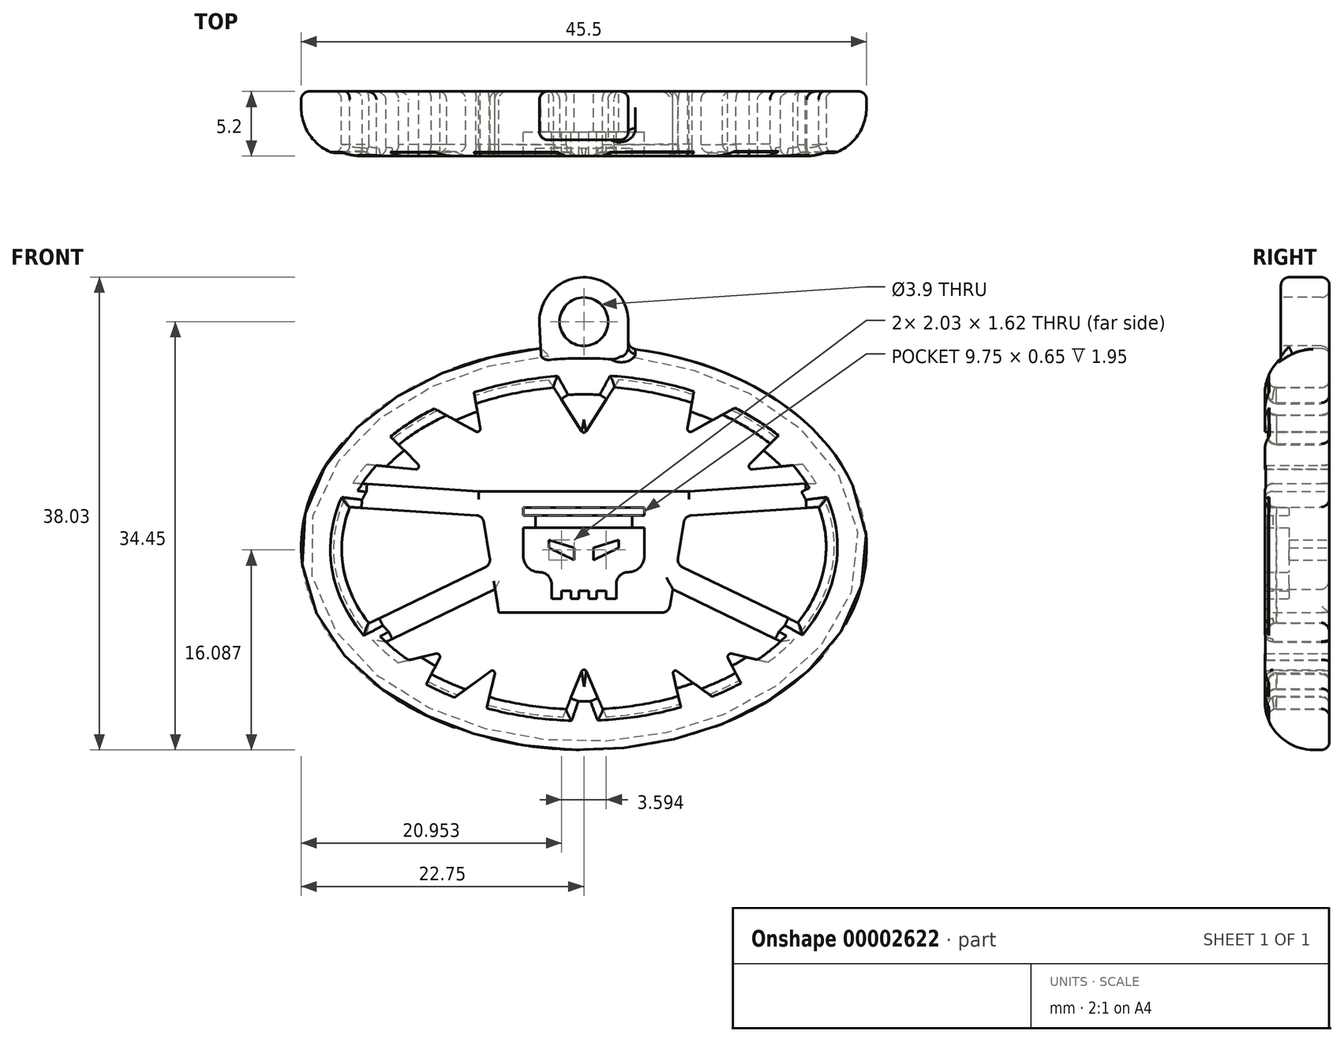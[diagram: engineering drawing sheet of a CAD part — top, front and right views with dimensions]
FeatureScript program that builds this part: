
annotation { "Feature Type Name" : "Feature", "Feature Type Description" : "" }
export const myFeature = defineFeature(function(context is Context, id is Id, definition is map)
    precondition{}
    {
        {
            var Q0;
            Q0=qCreatedBy(makeId("Front.planeOp"),FACE);
            var sketch = newSketch(context, id + "F0", { "sketchPlane" : qUnion([Q0])});
            skEllipse(sketch, "E0", {"center": v(0, 0) * mm, "majorRadius": 17.5 * mm, "minorRadius": 12.5 * mm, "majorAxis": v(1, 0)});
            skEllipticalArc(sketch, "E1", {});
            skLineSegment(sketch, "E2", {"start": v(-6.5, 3.5) * mm, "end": v(-5.27, -4) * mm});
            skLineSegment(sketch, "E3.0.MirrorCS", {"start": v(6.5, 3.5) * mm, "end": v(5.27, -4) * mm});
            skLineSegment(sketch, "E4", {"start": v(-6.5, 3.5) * mm, "end": v(6.5, 3.5) * mm});
            skLineSegment(sketch, "E5", {"start": v(-5.27, -4) * mm, "end": v(5.27, -4) * mm});
            skLineSegment(sketch, "E6", {"start": v(-5.5, -2.56) * mm, "end": v(-12.25, -5.82) * mm});
            skLineSegment(sketch, "E7", {"start": v(-13.3, -4.67) * mm, "end": v(-5.76, -1.02) * mm});
            skLineSegment(sketch, "E8", {"start": v(-6.5, 3.5) * mm, "end": v(-13.72, 3.98) * mm});
            skLineSegment(sketch, "E9", {"start": v(-6.25, 1.98) * mm, "end": v(-14.49, 2.53) * mm});
            skLineSegment(sketch, "E10.0.MirrorCS", {"start": v(6.5, 3.5) * mm, "end": v(13.72, 3.98) * mm});
            skLineSegment(sketch, "E11.0.MirrorCS", {"start": v(6.25, 1.98) * mm, "end": v(14.49, 2.53) * mm});
            skLineSegment(sketch, "E12.0.MirrorCS", {"start": v(13.3, -4.67) * mm, "end": v(5.76, -1.02) * mm});
            skLineSegment(sketch, "E13.0.MirrorCS", {"start": v(5.5, -2.56) * mm, "end": v(12.25, -5.82) * mm});
            skLineSegment(sketch, "E14", {"start": v(0, 2.5) * mm, "end": v(-3.75, 2.5) * mm});
            skLineSegment(sketch, "E15", {"start": v(-3.75, 2.5) * mm, "end": v(-3.75, 2) * mm});
            skLineSegment(sketch, "E16", {"start": v(-3.75, 2) * mm, "end": v(-3, 2) * mm});
            skLineSegment(sketch, "E17", {"start": v(-3, 2) * mm, "end": v(-3, 1.25) * mm});
            skLineSegment(sketch, "E18", {"start": v(-3, 1.25) * mm, "end": v(-3.75, 1.25) * mm});
            skLineSegment(sketch, "E19", {"start": v(-3.75, 1.25) * mm, "end": v(-3.75, -0.5) * mm});
            skLineSegment(sketch, "E20", {"start": v(-2.75, -1.5) * mm, "end": v(-2.75, -1.5) * mm});
            skLineSegment(sketch, "E21", {"start": v(-2, -2.25) * mm, "end": v(-2, -3.16) * mm});
            skLineSegment(sketch, "E22", {"start": v(-2, -3.16) * mm, "end": v(-1.39, -3.16) * mm});
            skLineSegment(sketch, "E23", {"start": v(0, -3.16) * mm, "end": v(0, 2.5) * mm});
            skPoint(sketch, "E24.visualSharp", {"position": v(-3.75, -1.5) * mm});
            skArc(sketch, "E24.filletArc", {"start": v(-3.75, -0.5) * mm, "mid": v(-3.46, -1.2) * mm, "end": v(-2.75, -1.5) * mm});
            skPoint(sketch, "E25.visualSharp", {"position": v(-2, -1.5) * mm});
            skArc(sketch, "E25.filletArc", {"start": v(-2, -2.25) * mm, "mid": v(-2.22, -1.72) * mm, "end": v(-2.75, -1.5) * mm});
            skLineSegment(sketch, "E26.0.MirrorCS", {"start": v(0, 2.5) * mm, "end": v(3.75, 2.5) * mm});
            skLineSegment(sketch, "E27.0.MirrorCS", {"start": v(3.75, 2.5) * mm, "end": v(3.75, 2) * mm});
            skLineSegment(sketch, "E28.0.MirrorCS", {"start": v(3.75, 2) * mm, "end": v(3, 2) * mm});
            skLineSegment(sketch, "E29.0.MirrorCS", {"start": v(3, 2) * mm, "end": v(3, 1.25) * mm});
            skLineSegment(sketch, "E30.0.MirrorCS", {"start": v(3.75, 1.25) * mm, "end": v(3.75, -0.5) * mm});
            skLineSegment(sketch, "E31.0.MirrorCS", {"start": v(3, 1.25) * mm, "end": v(3.75, 1.25) * mm});
            skArc(sketch, "E32.0.MirrorCS", {"start": v(3.75, -0.5) * mm, "mid": v(3.46, -1.2) * mm, "end": v(2.75, -1.5) * mm});
            skArc(sketch, "E33.0.MirrorCS", {"start": v(2, -2.25) * mm, "mid": v(2.22, -1.72) * mm, "end": v(2.75, -1.5) * mm});
            skLineSegment(sketch, "E34.0.MirrorCS", {"start": v(2, -3.16) * mm, "end": v(1.39, -3.16) * mm});
            skLineSegment(sketch, "E35.0.MirrorCS", {"start": v(2, -2.25) * mm, "end": v(2, -3.16) * mm});
            skLineSegment(sketch, "E36", {"start": v(-3, 1.25) * mm, "end": v(3, 1.25) * mm});
            skLineSegment(sketch, "E37", {"start": v(-3, 2) * mm, "end": v(3, 2) * mm});
            skLineSegment(sketch, "E38", {"start": v(-0.6, -0.75) * mm, "end": v(-0.6, 0) * mm});
            skLineSegment(sketch, "E39", {"start": v(-0.6, 0) * mm, "end": v(-2.16, 0.5) * mm});
            skLineSegment(sketch, "E40", {"start": v(-2.16, 0.5) * mm, "end": v(-2.16, 0) * mm});
            skLineSegment(sketch, "E41", {"start": v(-2.16, 0) * mm, "end": v(-0.6, -0.75) * mm});
            skLineSegment(sketch, "E42.0.MirrorCS", {"start": v(0.6, -0.75) * mm, "end": v(0.6, 0) * mm});
            skLineSegment(sketch, "E43.0.MirrorCS", {"start": v(0.6, 0) * mm, "end": v(2.16, 0.5) * mm});
            skLineSegment(sketch, "E44.0.MirrorCS", {"start": v(2.16, 0.5) * mm, "end": v(2.16, 0) * mm});
            skLineSegment(sketch, "E45.0.MirrorCS", {"start": v(2.16, 0) * mm, "end": v(0.6, -0.75) * mm});
            skLineSegment(sketch, "E46.rect.bottom", {"start": v(-0.79, -2.38) * mm, "end": v(-1.39, -2.38) * mm});
            skLineSegment(sketch, "E46.rect.left", {"start": v(-0.79, -2.65) * mm, "end": v(-0.79, -3.16) * mm});
            skLineSegment(sketch, "E46.rect.right", {"start": v(-1.39, -2.65) * mm, "end": v(-1.39, -3.16) * mm});
            skLineSegment(sketch, "E47.trimOffspring", {"start": v(-0.79, -3.16) * mm, "end": v(-0.3, -3.16) * mm});
            skLineSegment(sketch, "E48.0.MirrorCS", {"start": v(1.39, -2.65) * mm, "end": v(1.39, -3.16) * mm});
            skLineSegment(sketch, "E49.0.MirrorCS", {"start": v(0.79, -2.65) * mm, "end": v(0.79, -3.16) * mm});
            skLineSegment(sketch, "E50.trimOffspring", {"start": v(0.79, -3.16) * mm, "end": v(0.3, -3.16) * mm});
            skLineSegment(sketch, "E51.rect.bottom", {"start": v(-0.3, -2.38) * mm, "end": v(0.3, -2.38) * mm});
            skLineSegment(sketch, "E51.rect.left", {"start": v(-0.3, -2.65) * mm, "end": v(-0.3, -3.16) * mm});
            skLineSegment(sketch, "E51.rect.right", {"start": v(0.3, -2.65) * mm, "end": v(0.3, -3.16) * mm});
            skLineSegment(sketch, "E52", {"start": v(13.72, 3.98) * mm, "end": v(13.8, 3.98) * mm});
            skLineSegment(sketch, "E53", {"start": v(14.49, 2.53) * mm, "end": v(14.54, 2.53) * mm});
            skEllipticalArc(sketch, "E54.trimOffspring", {});
            skEllipticalArc(sketch, "E55.trimOffspring", {});
            skEllipticalArc(sketch, "E56.trimOffspring", {});
            skLineSegment(sketch, "E57", {"start": v(-6.68, 8.92) * mm, "end": v(-6.34, 7.01) * mm});
            skLineSegment(sketch, "E58", {"start": v(-6.34, 7.01) * mm, "end": v(-8.5, 8.2) * mm});
            skLineSegment(sketch, "E59", {"start": v(-12.85, 5.1) * mm, "end": v(-9.89, 4.8) * mm});
            skLineSegment(sketch, "E60", {"start": v(-9.89, 4.8) * mm, "end": v(-11.48, 6.39) * mm});
            skLineSegment(sketch, "E61", {"start": v(0, 7.01) * mm, "end": v(-1.86, 9.91) * mm});
            skLineSegment(sketch, "E62.0.MirrorCS", {"start": v(0, 7.01) * mm, "end": v(1.86, 9.91) * mm});
            skLineSegment(sketch, "E63.0.MirrorCS", {"start": v(6.68, 8.92) * mm, "end": v(6.34, 7.01) * mm});
            skLineSegment(sketch, "E64.0.MirrorCS", {"start": v(6.34, 7.01) * mm, "end": v(8.5, 8.2) * mm});
            skLineSegment(sketch, "E65.0.MirrorCS", {"start": v(9.89, 4.8) * mm, "end": v(11.48, 6.39) * mm});
            skLineSegment(sketch, "E66.0.MirrorCS", {"start": v(12.85, 5.1) * mm, "end": v(9.89, 4.8) * mm});
            skLineSegment(sketch, "E67", {"start": v(1.86, 9.91) * mm, "end": v(1.95, 10.06) * mm});
            skLineSegment(sketch, "E68", {"start": v(6.68, 8.92) * mm, "end": v(6.75, 9.33) * mm});
            skLineSegment(sketch, "E69", {"start": v(8.5, 8.2) * mm, "end": v(9, 8.47) * mm});
            skLineSegment(sketch, "E70", {"start": v(11.48, 6.39) * mm, "end": v(11.88, 6.8) * mm});
            skLineSegment(sketch, "E71", {"start": v(12.85, 5.1) * mm, "end": v(13.46, 5.17) * mm});
            skLineSegment(sketch, "E72", {"start": v(-10.85, -6.95) * mm, "end": v(-8.74, -6.45) * mm});
            skLineSegment(sketch, "E73", {"start": v(-8.74, -6.45) * mm, "end": v(-9.44, -7.81) * mm});
            skLineSegment(sketch, "E74", {"start": v(-7.32, -8.76) * mm, "end": v(-5.43, -7.38) * mm});
            skLineSegment(sketch, "E75", {"start": v(-5.43, -7.38) * mm, "end": v(-5.92, -9.51) * mm});
            skLineSegment(sketch, "E76", {"start": v(-1.08, -9.98) * mm, "end": v(0, -7.3) * mm});
            skLineSegment(sketch, "E77", {"start": v(0, -7.3) * mm, "end": v(1.16, -9.96) * mm});
            skLineSegment(sketch, "E78.0.MirrorCS", {"start": v(5.43, -7.38) * mm, "end": v(5.92, -9.51) * mm});
            skLineSegment(sketch, "E79.0.MirrorCS", {"start": v(7.32, -8.76) * mm, "end": v(5.43, -7.38) * mm});
            skLineSegment(sketch, "E80.0.MirrorCS", {"start": v(8.74, -6.45) * mm, "end": v(9.44, -7.81) * mm});
            skLineSegment(sketch, "E81.0.MirrorCS", {"start": v(10.85, -6.95) * mm, "end": v(8.74, -6.45) * mm});
            skArc(sketch, "E82", {"start": v(2.75, 14) * mm, "mid": v(-0.06, 16.75) * mm, "end": v(-2.75, 13.88) * mm});
            skLineSegment(sketch, "E83", {"start": v(-2.75, 13.88) * mm, "end": v(-2.68, 12.35) * mm});
            skLineSegment(sketch, "E84", {"start": v(2.75, 14) * mm, "end": v(2.75, 12.35) * mm});
            skLineSegment(sketch, "E85", {"start": v(-1.39, -2.65) * mm, "end": v(-0.79, -2.65) * mm});
            skLineSegment(sketch, "E86.trimOffspring", {"start": v(-0.3, -2.65) * mm, "end": v(0.3, -2.65) * mm});
            skLineSegment(sketch, "E87.trimOffspring", {"start": v(0.79, -2.65) * mm, "end": v(1.39, -2.65) * mm});
            skPoint(sketch, "E88.orphan", {"position": v(0.79, -2.38) * mm});
            skPoint(sketch, "E89.orphan", {"position": v(1.39, -2.38) * mm});
            const initialGuessF0  = {"E1": [0, 0, 0.9999678975144595, 0.008012736143888071, 0.015, 0.01, 2.8742552580067566, 3.615513402670112], "E54.trimOffspring": [0, 0, 0.9999678975144595, 0.008012736143888071, 0.015, 0.01, 3.751316391230873, 5.653974725832949], "E55.trimOffspring": [0, 0, 0.9999678975144595, 0.008012736143888071, 0.015, 0.01, 5.788912400985266, 0.24363722999687798], "E56.trimOffspring": [0, 0, 0.9999678975144595, 0.008012736143888071, 0.015, 0.01, 0.39710185617883087, 2.7204529747902204]};
            skSetInitialGuess(sketch, initialGuessF0);
            skSolve(sketch);
        }
        {
            var Q0;
            {var subQ8=sQuery(id+"F0.wireOp",EDGE,"E4");Q0=makeQuery(id+"F0.imprint","IMPRINT",FACE,{"disambiguationData":[TD([[makeQuery(id+"F0.imprint","IMPRINT",EDGE,{"derivedFrom":subQ8}),-1.0]])]});}
            var Q1;
            {var subQ1=sQuery(id+"F0.wireOp",EDGE,"E59");Q1=makeQuery(id+"F0.imprint","IMPRINT",FACE,{"disambiguationData":[TD([[makeQuery(id+"F0.imprint","IMPRINT",EDGE,{"derivedFrom":subQ1}),1.0]])]});}
            var Q2;
            {var subQ1=sQuery(id+"F0.wireOp",EDGE,"E57");Q2=makeQuery(id+"F0.imprint","IMPRINT",FACE,{"disambiguationData":[TD([[makeQuery(id+"F0.imprint","IMPRINT",EDGE,{"derivedFrom":subQ1}),-1.0]])]});}
            var Q3;
            {var subQ0=sQuery(id+"F0.wireOp",EDGE,"E61");Q3=makeQuery(id+"F0.imprint","IMPRINT",FACE,{"disambiguationData":[TD([[makeQuery(id+"F0.imprint","IMPRINT",EDGE,{"derivedFrom":subQ0}),-1.0]])]});}
            var Q4;
            {var subQ6=sQuery(id+"F0.wireOp",EDGE,"E63.0.MirrorCS");Q4=makeQuery(id+"F0.imprint","IMPRINT",FACE,{"disambiguationData":[TD([[makeQuery(id+"F0.imprint","IMPRINT",EDGE,{"derivedFrom":subQ6}),1.0]])]});}
            var Q5;
            {var subQ3=sQuery(id+"F0.wireOp",EDGE,"E65.0.MirrorCS");Q5=makeQuery(id+"F0.imprint","IMPRINT",FACE,{"disambiguationData":[TD([[makeQuery(id+"F0.imprint","IMPRINT",EDGE,{"derivedFrom":subQ3}),-1.0]])]});}
            var Q6;
            {var subQ1=sQuery(id+"F0.wireOp",EDGE,"E72");Q6=makeQuery(id+"F0.imprint","IMPRINT",FACE,{"disambiguationData":[TD([[makeQuery(id+"F0.imprint","IMPRINT",EDGE,{"derivedFrom":subQ1}),-1.0]])]});}
            var Q7;
            {var subQ3=sQuery(id+"F0.wireOp",EDGE,"E74");Q7=makeQuery(id+"F0.imprint","IMPRINT",FACE,{"disambiguationData":[TD([[makeQuery(id+"F0.imprint","IMPRINT",EDGE,{"derivedFrom":subQ3}),-1.0]])]});}
            var Q8;
            {var subQ1=sQuery(id+"F0.wireOp",EDGE,"E76");Q8=makeQuery(id+"F0.imprint","IMPRINT",FACE,{"disambiguationData":[TD([[makeQuery(id+"F0.imprint","IMPRINT",EDGE,{"derivedFrom":subQ1}),-1.0]])]});}
            var Q9;
            {var subQ1=sQuery(id+"F0.wireOp",EDGE,"E54.trimOffspring");var subQ3=sQuery(id+"F0.wireOp",EDGE,"E78.0.MirrorCS");var subQ5=makeQuery(id+"F0.imprint","INTERSECT",VERTEX,{"derivedFrom":[subQ1,subQ3]});Q9=makeQuery(id+"F0.imprint","IMPRINT",FACE,{"disambiguationData":[TD([[makeQuery(id+"F0.imprint","IMPRINT",EDGE,{"disambiguationData":[TD([[subQ5,-1.0]])],"derivedFrom":subQ1}),1.0]])]});}
            var Q10;
            {var subQ1=sQuery(id+"F0.wireOp",EDGE,"E54.trimOffspring");var subQ3=sQuery(id+"F0.wireOp",EDGE,"E80.0.MirrorCS");var subQ5=makeQuery(id+"F0.imprint","INTERSECT",VERTEX,{"derivedFrom":[subQ1,subQ3]});Q10=makeQuery(id+"F0.imprint","IMPRINT",FACE,{"disambiguationData":[TD([[makeQuery(id+"F0.imprint","IMPRINT",EDGE,{"disambiguationData":[TD([[subQ5,-1.0]])],"derivedFrom":subQ1}),1.0]])]});}
            var Q11;
            Q11=makeQuery(id+"F0.imprint","IMPRINT",FACE,{"disambiguationData":[TD([[makeQuery(id+"F0.imprint","IMPRINT",EDGE,{"derivedFrom":sQuery(id+"F0.wireOp",EDGE,"E1")}),-1.0]])]});
            var Q12;
            {var subQ1=sQuery(id+"F0.wireOp",EDGE,"E0");var subQ4=makeQuery(id+"F0.imprint","INTERSECT",VERTEX,{"derivedFrom":[subQ1,sQuery(id+"F0.wireOp",EDGE,"6e1ee741-4015-48c1-b213-584f40299b3e")]});Q12=makeQuery(id+"F0.imprint","IMPRINT",FACE,{"disambiguationData":[TD([[makeQuery(id+"F0.imprint","IMPRINT",EDGE,{"disambiguationData":[TD([[subQ4,1.0]])],"derivedFrom":subQ1}),1.0]])]});}
            extrude(context, id + "F1", {"entities" : qUnion([Q0, Q1, Q2, Q3, Q4, Q5, Q6, Q7, Q8, Q9, Q10, Q11, Q12]), "depth" : 4 * mm});
        }
        {
            var Q0;
            {var subQ6=sQuery(id+"F0.wireOp",EDGE,"E18");Q0=makeQuery(id+"F0.imprint","IMPRINT",FACE,{"disambiguationData":[TD([[makeQuery(id+"F0.imprint","IMPRINT",EDGE,{"derivedFrom":subQ6}),1.0]])]});}
            var Q1;
            Q1=makeQuery(id+"F0.imprint","IMPRINT",FACE,{"disambiguationData":[TD([[makeQuery(id+"F0.imprint","IMPRINT",EDGE,{"derivedFrom":sQuery(id+"F0.wireOp",EDGE,"E30.0.MirrorCS")}),-1.0]])]});
            var Q2;
            {var subQ1=sQuery(id+"F0.wireOp",EDGE,"E26.0.MirrorCS");Q2=makeQuery(id+"F0.imprint","IMPRINT",FACE,{"disambiguationData":[TD([[makeQuery(id+"F0.imprint","IMPRINT",EDGE,{"derivedFrom":subQ1}),-1.0]])]});}
            var Q3;
            {var subQ4=sQuery(id+"F0.wireOp",EDGE,"E14");Q3=makeQuery(id+"F0.imprint","IMPRINT",FACE,{"disambiguationData":[TD([[makeQuery(id+"F0.imprint","IMPRINT",EDGE,{"derivedFrom":subQ4}),1.0]])]});}
            extrude(context, id + "F2", {"entities" : qUnion([Q0, Q1, Q2, Q3]), "operationType" : NewBodyOperationType.ADD, "depth" : 2.5 * mm});
        }
        {
            var Q0;
            Q0=makeQuery(id+"F0.imprint","IMPRINT",FACE,{"disambiguationData":[TD([[makeQuery(id+"F0.imprint","IMPRINT",EDGE,{"derivedFrom":sQuery(id+"F0.wireOp",EDGE,"E82")}),1.0]])]});
            extrude(context, id + "F3", {"entities" : qUnion([Q0]), "operationType" : NewBodyOperationType.ADD, "depth" : 3 * mm});
        }
        {
            var Q0;
            Q0=makeQuery(id+"F3.opExtrude","CAP_FACE",FACE,{"disambiguationData":[OSD([sQuery(id+"F0.wireOp",EDGE,"E0"),sQuery(id+"F0.wireOp",EDGE,"E82"),sQuery(id+"F0.wireOp",EDGE,"E83"),sQuery(id+"F0.wireOp",EDGE,"E84")])],"isStart":false});
            var sketch = newSketch(context, id + "F4", { "sketchPlane" : qUnion([Q0])});
            skCircle(sketch, "E90", {"center": v(0, 14) * mm, "radius": 1.5 * mm});
            skSolve(sketch);
        }
        {
            var Q0;
            Q0=makeQuery(id+"F4.imprint","IMPRINT",FACE,{"disambiguationData":[TD([[makeQuery(id+"F4.imprint","IMPRINT",EDGE,{"derivedFrom":sQuery(id+"F4.wireOp",EDGE,"E90")}),1.0]])]});
            extrude(context, id + "F5", {"entities" : qUnion([Q0]), "operationType" : NewBodyOperationType.REMOVE, "oppositeDirection" : true, "depth" : 25 * mm});
        }
        {
            var Q0;
            Q0=makeQuery(id+"F1.opExtrude","CAP_EDGE",EDGE,{"disambiguationData":[OSD([sQuery(id+"F0.wireOp",EDGE,"E0")])],"isStart":false});
            fillet(context, id + "F6", {"entities" : qUnion([Q0]), "radius" : 3 * mm, "tangentPropagation" : true, "allowEdgeOverflow" : false});
        }
        {
            var Q0;
            Q0=makeQuery(id+"F1.opExtrude","CAP_EDGE",EDGE,{"disambiguationData":[OSD([sQuery(id+"F0.wireOp",EDGE,"E0")])],"isStart":true});
            var Q1;
            Q1=makeQuery(id+"F3.opExtrude","CAP_EDGE",EDGE,{"disambiguationData":[OSD([sQuery(id+"F0.wireOp",EDGE,"E82")])],"isStart":true});
            var Q2;
            Q2=makeQuery(id+"F3.opExtrude","CAP_EDGE",EDGE,{"disambiguationData":[OSD([sQuery(id+"F0.wireOp",EDGE,"E84")])],"isStart":true});
            var Q3;
            Q3=makeQuery(id+"F3.opExtrude","CAP_EDGE",EDGE,{"disambiguationData":[OSD([sQuery(id+"F0.wireOp",EDGE,"E83")])],"isStart":true});
            var Q4;
            Q4=makeQuery(id+"F3.opExtrude","CAP_EDGE",EDGE,{"disambiguationData":[OSD([sQuery(id+"F0.wireOp",EDGE,"E82")])],"isStart":false});
            var Q5;
            Q5=makeQuery(id+"F3.opExtrude","CAP_EDGE",EDGE,{"disambiguationData":[OSD([sQuery(id+"F0.wireOp",EDGE,"E84")])],"isStart":false});
            var Q6;
            Q6=makeQuery(id+"F6.opFillet","BLEND_EDGE",EDGE,{"blendedFrom":[makeQuery(id+"F1.opExtrude","CAP_EDGE",EDGE,{"disambiguationData":[OSD([sQuery(id+"F0.wireOp",EDGE,"E0")])],"isStart":false}),makeQuery(id+"F3.opExtrude","SWEPT_FACE",FACE,{"disambiguationData":[OSD([sQuery(id+"F0.wireOp",EDGE,"E84")])]})],"blendedInto":[makeQuery(id+"F3.opExtrude","SWEPT_FACE",FACE,{"disambiguationData":[OSD([sQuery(id+"F0.wireOp",EDGE,"E84")])]})]});
            var Q7;
            {var subQ0=sQuery(id+"F0.wireOp",EDGE,"E0");var subQ1=sQuery(id+"F0.wireOp",EDGE,"E14");var subQ2=sQuery(id+"F0.wireOp",EDGE,"E15");var subQ3=sQuery(id+"F0.wireOp",EDGE,"E16");var subQ4=sQuery(id+"F0.wireOp",EDGE,"E18");var subQ5=sQuery(id+"F0.wireOp",EDGE,"E19");var subQ6=sQuery(id+"F0.wireOp",EDGE,"E21");var subQ7=sQuery(id+"F0.wireOp",EDGE,"E22");var subQ8=sQuery(id+"F0.wireOp",EDGE,"E24.filletArc");var subQ9=sQuery(id+"F0.wireOp",EDGE,"E25.filletArc");var subQ10=sQuery(id+"F0.wireOp",EDGE,"E26.0.MirrorCS");var subQ11=sQuery(id+"F0.wireOp",EDGE,"E27.0.MirrorCS");var subQ12=sQuery(id+"F0.wireOp",EDGE,"E28.0.MirrorCS");var subQ13=sQuery(id+"F0.wireOp",EDGE,"E30.0.MirrorCS");var subQ14=sQuery(id+"F0.wireOp",EDGE,"E31.0.MirrorCS");var subQ15=sQuery(id+"F0.wireOp",EDGE,"E32.0.MirrorCS");var subQ16=sQuery(id+"F0.wireOp",EDGE,"E33.0.MirrorCS");var subQ17=sQuery(id+"F0.wireOp",EDGE,"E34.0.MirrorCS");var subQ18=sQuery(id+"F0.wireOp",EDGE,"E35.0.MirrorCS");var subQ19=sQuery(id+"F0.wireOp",EDGE,"E46.rect.left");var subQ20=sQuery(id+"F0.wireOp",EDGE,"E46.rect.right");var subQ21=sQuery(id+"F0.wireOp",EDGE,"E47.trimOffspring");var subQ22=sQuery(id+"F0.wireOp",EDGE,"E48.0.MirrorCS");var subQ23=sQuery(id+"F0.wireOp",EDGE,"E49.0.MirrorCS");var subQ24=sQuery(id+"F0.wireOp",EDGE,"E50.trimOffspring");var subQ25=sQuery(id+"F0.wireOp",EDGE,"E51.rect.left");var subQ26=sQuery(id+"F0.wireOp",EDGE,"E51.rect.right");var subQ27=sQuery(id+"F0.wireOp",EDGE,"E85");var subQ28=sQuery(id+"F0.wireOp",EDGE,"E86.trimOffspring");var subQ29=sQuery(id+"F0.wireOp",EDGE,"E87.trimOffspring");Q7=makeQuery(id+"F5.boolean.opBoolean","INTERSECT",EDGE,{"derivedFrom":[makeQuery(id+"F3.boolean.opBoolean","MERGE",FACE,{"derivedFrom":[makeQuery(id+"F2.boolean.opBoolean","MERGE",FACE,{"derivedFrom":[makeQuery(id+"F1.opExtrude","CAP_FACE",FACE,{"disambiguationData":[OSD([subQ0,sQuery(id+"F0.wireOp",EDGE,"E1"),sQuery(id+"F0.wireOp",EDGE,"E2"),sQuery(id+"F0.wireOp",EDGE,"E3.0.MirrorCS"),sQuery(id+"F0.wireOp",EDGE,"E4"),sQuery(id+"F0.wireOp",EDGE,"E5"),sQuery(id+"F0.wireOp",EDGE,"E6"),sQuery(id+"F0.wireOp",EDGE,"E7"),sQuery(id+"F0.wireOp",EDGE,"E8"),sQuery(id+"F0.wireOp",EDGE,"E9"),sQuery(id+"F0.wireOp",EDGE,"E10.0.MirrorCS"),sQuery(id+"F0.wireOp",EDGE,"E11.0.MirrorCS"),sQuery(id+"F0.wireOp",EDGE,"E12.0.MirrorCS"),sQuery(id+"F0.wireOp",EDGE,"E13.0.MirrorCS"),subQ1,subQ2,subQ3,sQuery(id+"F0.wireOp",EDGE,"E17"),subQ4,subQ5,subQ6,subQ7,subQ8,subQ9,subQ10,subQ11,subQ12,sQuery(id+"F0.wireOp",EDGE,"E29.0.MirrorCS"),subQ13,subQ14,subQ15,subQ16,subQ17,subQ18,subQ19,subQ20,subQ21,subQ22,subQ23,subQ24,subQ25,subQ26,sQuery(id+"F0.wireOp",EDGE,"E52"),sQuery(id+"F0.wireOp",EDGE,"E53"),sQuery(id+"F0.wireOp",EDGE,"E54.trimOffspring"),sQuery(id+"F0.wireOp",EDGE,"E55.trimOffspring"),sQuery(id+"F0.wireOp",EDGE,"E56.trimOffspring"),sQuery(id+"F0.wireOp",EDGE,"E57"),sQuery(id+"F0.wireOp",EDGE,"E58"),sQuery(id+"F0.wireOp",EDGE,"E59"),sQuery(id+"F0.wireOp",EDGE,"E60"),sQuery(id+"F0.wireOp",EDGE,"E61"),sQuery(id+"F0.wireOp",EDGE,"E62.0.MirrorCS"),sQuery(id+"F0.wireOp",EDGE,"E63.0.MirrorCS"),sQuery(id+"F0.wireOp",EDGE,"E64.0.MirrorCS"),sQuery(id+"F0.wireOp",EDGE,"E65.0.MirrorCS"),sQuery(id+"F0.wireOp",EDGE,"E66.0.MirrorCS"),sQuery(id+"F0.wireOp",EDGE,"E67"),sQuery(id+"F0.wireOp",EDGE,"E68"),sQuery(id+"F0.wireOp",EDGE,"E69"),sQuery(id+"F0.wireOp",EDGE,"E70"),sQuery(id+"F0.wireOp",EDGE,"E71"),sQuery(id+"F0.wireOp",EDGE,"E72"),sQuery(id+"F0.wireOp",EDGE,"E73"),sQuery(id+"F0.wireOp",EDGE,"E74"),sQuery(id+"F0.wireOp",EDGE,"E75"),sQuery(id+"F0.wireOp",EDGE,"E76"),sQuery(id+"F0.wireOp",EDGE,"E77"),sQuery(id+"F0.wireOp",EDGE,"E78.0.MirrorCS"),sQuery(id+"F0.wireOp",EDGE,"E79.0.MirrorCS"),sQuery(id+"F0.wireOp",EDGE,"E80.0.MirrorCS"),sQuery(id+"F0.wireOp",EDGE,"E81.0.MirrorCS"),subQ27,subQ28,subQ29])],"isStart":true}),makeQuery(id+"F2.opExtrude","CAP_FACE",FACE,{"disambiguationData":[OSD([subQ1,subQ2,subQ3,subQ10,subQ11,subQ12,sQuery(id+"F0.wireOp",EDGE,"E37")])],"isStart":true}),makeQuery(id+"F2.opExtrude","CAP_FACE",FACE,{"disambiguationData":[OSD([subQ4,subQ5,subQ6,subQ7,subQ8,subQ9,subQ13,subQ14,subQ15,subQ16,subQ17,subQ18,sQuery(id+"F0.wireOp",EDGE,"E36"),sQuery(id+"F0.wireOp",EDGE,"E38"),sQuery(id+"F0.wireOp",EDGE,"E39"),sQuery(id+"F0.wireOp",EDGE,"E40"),sQuery(id+"F0.wireOp",EDGE,"E41"),sQuery(id+"F0.wireOp",EDGE,"E42.0.MirrorCS"),sQuery(id+"F0.wireOp",EDGE,"E43.0.MirrorCS"),sQuery(id+"F0.wireOp",EDGE,"E44.0.MirrorCS"),sQuery(id+"F0.wireOp",EDGE,"E45.0.MirrorCS"),subQ19,subQ20,subQ21,subQ22,subQ23,subQ24,subQ25,subQ26,subQ27,subQ28,subQ29])],"isStart":true})]}),makeQuery(id+"F3.opExtrude","CAP_FACE",FACE,{"disambiguationData":[OSD([subQ0,sQuery(id+"F0.wireOp",EDGE,"E82"),sQuery(id+"F0.wireOp",EDGE,"E83"),sQuery(id+"F0.wireOp",EDGE,"E84")])],"isStart":true})]}),makeQuery(id+"F5.opExtrude","SWEPT_FACE",FACE,{"disambiguationData":[OSD([sQuery(id+"F4.wireOp",EDGE,"E90")])]})]});}
            var Q8;
            Q8=makeQuery(id+"F5.boolean.opBoolean","COPY",EDGE,{"derivedFrom":makeQuery(id+"F5.opExtrude","CAP_EDGE",EDGE,{"disambiguationData":[OSD([sQuery(id+"F4.wireOp",EDGE,"E90")])],"isStart":true})});
            var Q9;
            Q9=makeQuery(id+"F1.opExtrude","CAP_EDGE",EDGE,{"disambiguationData":[OSD([sQuery(id+"F0.wireOp",EDGE,"E7")])],"isStart":false});
            var Q10;
            Q10=makeQuery(id+"F1.opExtrude","CAP_EDGE",EDGE,{"disambiguationData":[OSD([sQuery(id+"F0.wireOp",EDGE,"E9")])],"isStart":true});
            var Q11;
            Q11=makeQuery(id+"F1.opExtrude","CAP_EDGE",EDGE,{"disambiguationData":[OSD([sQuery(id+"F0.wireOp",EDGE,"E8")])],"isStart":false});
            var Q12;
            Q12=makeQuery(id+"F1.opExtrude","CAP_EDGE",EDGE,{"disambiguationData":[OSD([sQuery(id+"F0.wireOp",EDGE,"E4")])],"isStart":false});
            var Q13;
            Q13=makeQuery(id+"F1.opExtrude","CAP_EDGE",EDGE,{"disambiguationData":[OSD([sQuery(id+"F0.wireOp",EDGE,"E10.0.MirrorCS")])],"isStart":false});
            var Q14;
            Q14=makeQuery(id+"F1.opExtrude","CAP_EDGE",EDGE,{"disambiguationData":[OSD([sQuery(id+"F0.wireOp",EDGE,"E11.0.MirrorCS"),sQuery(id+"F0.wireOp",EDGE,"E53")])],"isStart":false});
            var Q15;
            {var subQ0=sQuery(id+"F0.wireOp",EDGE,"E3.0.MirrorCS");Q15=makeQuery(id+"F1.opExtrude","CAP_EDGE",EDGE,{"disambiguationData":[OSD([subQ0]),TDD([makeQuery(id+"F0.imprint","IMPRINT",EDGE,{"disambiguationData":[TD([[makeQuery(id+"F0.imprint","INTERSECT",VERTEX,{"derivedFrom":[subQ0,sQuery(id+"F0.wireOp",EDGE,"E11.0.MirrorCS")]}),-1.0]])],"derivedFrom":subQ0})])],"isStart":false});}
            var Q16;
            Q16=makeQuery(id+"F1.opExtrude","CAP_EDGE",EDGE,{"disambiguationData":[OSD([sQuery(id+"F0.wireOp",EDGE,"E12.0.MirrorCS")])],"isStart":true});
            var Q17;
            Q17=makeQuery(id+"F1.opExtrude","CAP_EDGE",EDGE,{"disambiguationData":[OSD([sQuery(id+"F0.wireOp",EDGE,"E13.0.MirrorCS")])],"isStart":false});
            var Q18;
            {var subQ0=sQuery(id+"F0.wireOp",EDGE,"E3.0.MirrorCS");Q18=makeQuery(id+"F1.opExtrude","CAP_EDGE",EDGE,{"disambiguationData":[OSD([subQ0]),TDD([makeQuery(id+"F0.imprint","IMPRINT",EDGE,{"disambiguationData":[TD([[makeQuery(id+"F0.imprint","INTERSECT",VERTEX,{"derivedFrom":[subQ0,sQuery(id+"F0.wireOp",EDGE,"E5")]}),1.0]])],"derivedFrom":subQ0})])],"isStart":false});}
            var Q19;
            Q19=makeQuery(id+"F1.opExtrude","CAP_EDGE",EDGE,{"disambiguationData":[OSD([sQuery(id+"F0.wireOp",EDGE,"E5")])],"isStart":false});
            var Q20;
            Q20=makeQuery(id+"F1.opExtrude","SWEPT_EDGE",EDGE,{"disambiguationData":[OSD([sQuery(id+"F0.wireOp",EDGE,"E3.0.MirrorCS"),sQuery(id+"F0.wireOp",EDGE,"E5")])]});
            var Q21;
            {var subQ0=sQuery(id+"F0.wireOp",EDGE,"E3.0.MirrorCS");Q21=makeQuery(id+"F1.opExtrude","CAP_EDGE",EDGE,{"disambiguationData":[OSD([subQ0]),TDD([makeQuery(id+"F0.imprint","IMPRINT",EDGE,{"disambiguationData":[TD([[makeQuery(id+"F0.imprint","INTERSECT",VERTEX,{"derivedFrom":[subQ0,sQuery(id+"F0.wireOp",EDGE,"E11.0.MirrorCS")]}),-1.0]])],"derivedFrom":subQ0})])],"isStart":true});}
            var Q22;
            {var subQ0=sQuery(id+"F0.wireOp",EDGE,"E3.0.MirrorCS");Q22=makeQuery(id+"F1.opExtrude","CAP_EDGE",EDGE,{"disambiguationData":[OSD([subQ0]),TDD([makeQuery(id+"F0.imprint","IMPRINT",EDGE,{"disambiguationData":[TD([[makeQuery(id+"F0.imprint","INTERSECT",VERTEX,{"derivedFrom":[subQ0,sQuery(id+"F0.wireOp",EDGE,"E5")]}),1.0]])],"derivedFrom":subQ0})])],"isStart":true});}
            var Q23;
            Q23=makeQuery(id+"F1.opExtrude","CAP_EDGE",EDGE,{"disambiguationData":[OSD([sQuery(id+"F0.wireOp",EDGE,"E6")])],"isStart":true});
            var Q24;
            Q24=makeQuery(id+"F1.opExtrude","CAP_EDGE",EDGE,{"disambiguationData":[OSD([sQuery(id+"F0.wireOp",EDGE,"E6")])],"isStart":false});
            var Q25;
            Q25=makeQuery(id+"F1.opExtrude","CAP_EDGE",EDGE,{"disambiguationData":[OSD([sQuery(id+"F0.wireOp",EDGE,"E11.0.MirrorCS"),sQuery(id+"F0.wireOp",EDGE,"E53")])],"isStart":true});
            var Q26;
            Q26=makeQuery(id+"F6.opFillet","BLEND_EDGE",EDGE,{"blendedFrom":[makeQuery(id+"F1.opExtrude","CAP_EDGE",EDGE,{"disambiguationData":[OSD([sQuery(id+"F0.wireOp",EDGE,"E0")])],"isStart":false}),makeQuery(id+"F1.opExtrude","SWEPT_FACE",FACE,{"disambiguationData":[OSD([sQuery(id+"F0.wireOp",EDGE,"E55.trimOffspring")])]})],"blendedInto":[makeQuery(id+"F1.opExtrude","SWEPT_FACE",FACE,{"disambiguationData":[OSD([sQuery(id+"F0.wireOp",EDGE,"E55.trimOffspring")])]})]});
            var Q27;
            Q27=makeQuery(id+"F1.opExtrude","CAP_EDGE",EDGE,{"disambiguationData":[OSD([sQuery(id+"F0.wireOp",EDGE,"E12.0.MirrorCS")])],"isStart":false});
            var Q28;
            Q28=makeQuery(id+"F1.opExtrude","CAP_EDGE",EDGE,{"disambiguationData":[OSD([sQuery(id+"F0.wireOp",EDGE,"E9")])],"isStart":false});
            var Q29;
            Q29=makeQuery(id+"F1.opExtrude","CAP_EDGE",EDGE,{"disambiguationData":[OSD([sQuery(id+"F0.wireOp",EDGE,"E7")])],"isStart":true});
            var Q30;
            Q30=makeQuery(id+"F1.opExtrude","CAP_EDGE",EDGE,{"disambiguationData":[OSD([sQuery(id+"F0.wireOp",EDGE,"E55.trimOffspring")])],"isStart":true});
            var Q31;
            {var subQ0=sQuery(id+"F0.wireOp",EDGE,"E56.trimOffspring");Q31=makeQuery(id+"F1.opExtrude","CAP_EDGE",EDGE,{"disambiguationData":[OSD([subQ0]),TDD([makeQuery(id+"F0.imprint","IMPRINT",EDGE,{"disambiguationData":[TD([[makeQuery(id+"F0.imprint","INTERSECT",VERTEX,{"derivedFrom":[subQ0,sQuery(id+"F0.wireOp",EDGE,"E70")]}),-1.0]])],"derivedFrom":subQ0})])],"isStart":true});}
            var Q32;
            {var subQ0=sQuery(id+"F0.wireOp",EDGE,"E56.trimOffspring");Q32=makeQuery(id+"F1.opExtrude","CAP_EDGE",EDGE,{"disambiguationData":[OSD([subQ0]),TDD([makeQuery(id+"F0.imprint","IMPRINT",EDGE,{"disambiguationData":[TD([[makeQuery(id+"F0.imprint","INTERSECT",VERTEX,{"derivedFrom":[subQ0,sQuery(id+"F0.wireOp",EDGE,"E68")]}),-1.0]])],"derivedFrom":subQ0})])],"isStart":true});}
            var Q33;
            {var subQ0=sQuery(id+"F0.wireOp",EDGE,"E56.trimOffspring");Q33=makeQuery(id+"F1.opExtrude","CAP_EDGE",EDGE,{"disambiguationData":[OSD([subQ0]),TDD([makeQuery(id+"F0.imprint","IMPRINT",EDGE,{"disambiguationData":[TD([[makeQuery(id+"F0.imprint","INTERSECT",VERTEX,{"derivedFrom":[subQ0,sQuery(id+"F0.wireOp",EDGE,"E57")]}),1.0]])],"derivedFrom":subQ0})])],"isStart":true});}
            var Q34;
            {var subQ0=sQuery(id+"F0.wireOp",EDGE,"E56.trimOffspring");Q34=makeQuery(id+"F1.opExtrude","CAP_EDGE",EDGE,{"disambiguationData":[OSD([subQ0]),TDD([makeQuery(id+"F0.imprint","IMPRINT",EDGE,{"disambiguationData":[TD([[makeQuery(id+"F0.imprint","INTERSECT",VERTEX,{"derivedFrom":[subQ0,sQuery(id+"F0.wireOp",EDGE,"E58")]}),-1.0]])],"derivedFrom":subQ0})])],"isStart":true});}
            var Q35;
            {var subQ0=sQuery(id+"F0.wireOp",EDGE,"E56.trimOffspring");Q35=makeQuery(id+"F1.opExtrude","CAP_EDGE",EDGE,{"disambiguationData":[OSD([subQ0]),TDD([makeQuery(id+"F0.imprint","IMPRINT",EDGE,{"disambiguationData":[TD([[makeQuery(id+"F0.imprint","INTERSECT",VERTEX,{"derivedFrom":[sQuery(id+"F0.wireOp",EDGE,"E8"),subQ0]}),1.0]])],"derivedFrom":subQ0})])],"isStart":true});}
            var Q36;
            {var subQ0=sQuery(id+"F0.wireOp",EDGE,"E56.trimOffspring");Q36=makeQuery(id+"F1.opExtrude","CAP_EDGE",EDGE,{"disambiguationData":[OSD([subQ0]),TDD([makeQuery(id+"F0.imprint","IMPRINT",EDGE,{"disambiguationData":[TD([[makeQuery(id+"F0.imprint","INTERSECT",VERTEX,{"derivedFrom":[sQuery(id+"F0.wireOp",EDGE,"E52"),subQ0]}),-1.0]])],"derivedFrom":subQ0})])],"isStart":true});}
            var Q37;
            {var subQ0=sQuery(id+"F0.wireOp",EDGE,"E54.trimOffspring");Q37=makeQuery(id+"F1.opExtrude","CAP_EDGE",EDGE,{"disambiguationData":[OSD([subQ0]),TDD([makeQuery(id+"F0.imprint","IMPRINT",EDGE,{"disambiguationData":[TD([[makeQuery(id+"F0.imprint","INTERSECT",VERTEX,{"derivedFrom":[sQuery(id+"F0.wireOp",EDGE,"E13.0.MirrorCS"),subQ0]}),1.0]])],"derivedFrom":subQ0})])],"isStart":true});}
            var Q38;
            {var subQ0=sQuery(id+"F0.wireOp",EDGE,"E54.trimOffspring");Q38=makeQuery(id+"F1.opExtrude","CAP_EDGE",EDGE,{"disambiguationData":[OSD([subQ0]),TDD([makeQuery(id+"F0.imprint","IMPRINT",EDGE,{"disambiguationData":[TD([[makeQuery(id+"F0.imprint","INTERSECT",VERTEX,{"derivedFrom":[subQ0,sQuery(id+"F0.wireOp",EDGE,"E79.0.MirrorCS")]}),-1.0]])],"derivedFrom":subQ0})])],"isStart":true});}
            var Q39;
            {var subQ0=sQuery(id+"F0.wireOp",EDGE,"E54.trimOffspring");Q39=makeQuery(id+"F1.opExtrude","CAP_EDGE",EDGE,{"disambiguationData":[OSD([subQ0]),TDD([makeQuery(id+"F0.imprint","IMPRINT",EDGE,{"disambiguationData":[TD([[makeQuery(id+"F0.imprint","INTERSECT",VERTEX,{"derivedFrom":[subQ0,sQuery(id+"F0.wireOp",EDGE,"E77")]}),-1.0]])],"derivedFrom":subQ0})])],"isStart":true});}
            var Q40;
            {var subQ0=sQuery(id+"F0.wireOp",EDGE,"E54.trimOffspring");Q40=makeQuery(id+"F1.opExtrude","CAP_EDGE",EDGE,{"disambiguationData":[OSD([subQ0]),TDD([makeQuery(id+"F0.imprint","IMPRINT",EDGE,{"disambiguationData":[TD([[makeQuery(id+"F0.imprint","INTERSECT",VERTEX,{"derivedFrom":[subQ0,sQuery(id+"F0.wireOp",EDGE,"E76")]}),1.0]])],"derivedFrom":subQ0})])],"isStart":true});}
            var Q41;
            {var subQ0=sQuery(id+"F0.wireOp",EDGE,"E54.trimOffspring");Q41=makeQuery(id+"F1.opExtrude","CAP_EDGE",EDGE,{"disambiguationData":[OSD([subQ0]),TDD([makeQuery(id+"F0.imprint","IMPRINT",EDGE,{"disambiguationData":[TD([[makeQuery(id+"F0.imprint","INTERSECT",VERTEX,{"derivedFrom":[subQ0,sQuery(id+"F0.wireOp",EDGE,"E73")]}),-1.0]])],"derivedFrom":subQ0})])],"isStart":true});}
            var Q42;
            {var subQ0=sQuery(id+"F0.wireOp",EDGE,"E54.trimOffspring");Q42=makeQuery(id+"F1.opExtrude","CAP_EDGE",EDGE,{"disambiguationData":[OSD([subQ0]),TDD([makeQuery(id+"F0.imprint","IMPRINT",EDGE,{"disambiguationData":[TD([[makeQuery(id+"F0.imprint","INTERSECT",VERTEX,{"derivedFrom":[sQuery(id+"F0.wireOp",EDGE,"E6"),subQ0]}),-1.0]])],"derivedFrom":subQ0})])],"isStart":true});}
            var Q43;
            Q43=makeQuery(id+"F1.opExtrude","CAP_EDGE",EDGE,{"disambiguationData":[OSD([sQuery(id+"F0.wireOp",EDGE,"E1")])],"isStart":true});
            var Q44;
            Q44=makeQuery(id+"F1.opExtrude","CAP_EDGE",EDGE,{"disambiguationData":[OSD([sQuery(id+"F0.wireOp",EDGE,"E13.0.MirrorCS")])],"isStart":true});
            var Q45;
            {var subQ0=sQuery(id+"F0.wireOp",EDGE,"E2");Q45=makeQuery(id+"F1.opExtrude","CAP_EDGE",EDGE,{"disambiguationData":[OSD([subQ0]),TDD([makeQuery(id+"F0.imprint","IMPRINT",EDGE,{"disambiguationData":[TD([[makeQuery(id+"F0.imprint","INTERSECT",VERTEX,{"derivedFrom":[subQ0,sQuery(id+"F0.wireOp",EDGE,"E5")]}),1.0]])],"derivedFrom":subQ0})])],"isStart":true});}
            var Q46;
            {var subQ0=sQuery(id+"F0.wireOp",EDGE,"E2");Q46=makeQuery(id+"F1.opExtrude","CAP_EDGE",EDGE,{"disambiguationData":[OSD([subQ0]),TDD([makeQuery(id+"F0.imprint","IMPRINT",EDGE,{"disambiguationData":[TD([[makeQuery(id+"F0.imprint","INTERSECT",VERTEX,{"derivedFrom":[subQ0,sQuery(id+"F0.wireOp",EDGE,"E7")]}),1.0]])],"derivedFrom":subQ0})])],"isStart":true});}
            var Q47;
            {var subQ0=sQuery(id+"F0.wireOp",EDGE,"E2");Q47=makeQuery(id+"F1.opExtrude","CAP_EDGE",EDGE,{"disambiguationData":[OSD([subQ0]),TDD([makeQuery(id+"F0.imprint","IMPRINT",EDGE,{"disambiguationData":[TD([[makeQuery(id+"F0.imprint","INTERSECT",VERTEX,{"derivedFrom":[subQ0,sQuery(id+"F0.wireOp",EDGE,"E7")]}),1.0]])],"derivedFrom":subQ0})])],"isStart":false});}
            var Q48;
            Q48=makeQuery(id+"F1.opExtrude","SWEPT_EDGE",EDGE,{"disambiguationData":[OSD([sQuery(id+"F0.wireOp",EDGE,"E2"),sQuery(id+"F0.wireOp",EDGE,"E7")])]});
            var Q49;
            Q49=makeQuery(id+"F1.opExtrude","SWEPT_EDGE",EDGE,{"disambiguationData":[OSD([sQuery(id+"F0.wireOp",EDGE,"E3.0.MirrorCS"),sQuery(id+"F0.wireOp",EDGE,"E12.0.MirrorCS")])]});
            var Q50;
            Q50=makeQuery(id+"F1.opExtrude","SWEPT_EDGE",EDGE,{"disambiguationData":[OSD([sQuery(id+"F0.wireOp",EDGE,"E3.0.MirrorCS"),sQuery(id+"F0.wireOp",EDGE,"E11.0.MirrorCS")])]});
            var Q51;
            Q51=makeQuery(id+"F1.opExtrude","SWEPT_EDGE",EDGE,{"disambiguationData":[OSD([sQuery(id+"F0.wireOp",EDGE,"E2"),sQuery(id+"F0.wireOp",EDGE,"E9")])]});
            var Q52;
            {var subQ0=sQuery(id+"F0.wireOp",EDGE,"E56.trimOffspring");Q52=makeQuery(id+"F6.opFillet","BLEND_EDGE",EDGE,{"blendedFrom":[makeQuery(id+"F1.opExtrude","CAP_EDGE",EDGE,{"disambiguationData":[OSD([sQuery(id+"F0.wireOp",EDGE,"E0")])],"isStart":false}),makeQuery(id+"F1.opExtrude","SWEPT_FACE",FACE,{"disambiguationData":[OSD([subQ0]),TDD([makeQuery(id+"F0.imprint","IMPRINT",EDGE,{"disambiguationData":[TD([[makeQuery(id+"F0.imprint","INTERSECT",VERTEX,{"derivedFrom":[subQ0,sQuery(id+"F0.wireOp",EDGE,"E58")]}),-1.0]])],"derivedFrom":subQ0})])]})],"blendedInto":[makeQuery(id+"F1.opExtrude","SWEPT_FACE",FACE,{"disambiguationData":[OSD([subQ0]),TDD([makeQuery(id+"F0.imprint","IMPRINT",EDGE,{"disambiguationData":[TD([[makeQuery(id+"F0.imprint","INTERSECT",VERTEX,{"derivedFrom":[subQ0,sQuery(id+"F0.wireOp",EDGE,"E58")]}),-1.0]])],"derivedFrom":subQ0})])]})]});}
            var Q53;
            {var subQ0=sQuery(id+"F0.wireOp",EDGE,"E56.trimOffspring");Q53=makeQuery(id+"F6.opFillet","BLEND_EDGE",EDGE,{"blendedFrom":[makeQuery(id+"F1.opExtrude","CAP_EDGE",EDGE,{"disambiguationData":[OSD([sQuery(id+"F0.wireOp",EDGE,"E0")])],"isStart":false}),makeQuery(id+"F1.opExtrude","SWEPT_FACE",FACE,{"disambiguationData":[OSD([subQ0]),TDD([makeQuery(id+"F0.imprint","IMPRINT",EDGE,{"disambiguationData":[TD([[makeQuery(id+"F0.imprint","INTERSECT",VERTEX,{"derivedFrom":[subQ0,sQuery(id+"F0.wireOp",EDGE,"E57")]}),1.0]])],"derivedFrom":subQ0})])]})],"blendedInto":[makeQuery(id+"F1.opExtrude","SWEPT_FACE",FACE,{"disambiguationData":[OSD([subQ0]),TDD([makeQuery(id+"F0.imprint","IMPRINT",EDGE,{"disambiguationData":[TD([[makeQuery(id+"F0.imprint","INTERSECT",VERTEX,{"derivedFrom":[subQ0,sQuery(id+"F0.wireOp",EDGE,"E57")]}),1.0]])],"derivedFrom":subQ0})])]})]});}
            var Q54;
            Q54=makeQuery(id+"F1.opExtrude","CAP_EDGE",EDGE,{"disambiguationData":[OSD([sQuery(id+"F0.wireOp",EDGE,"E61")])],"isStart":false});
            var Q55;
            Q55=makeQuery(id+"F1.opExtrude","CAP_EDGE",EDGE,{"disambiguationData":[OSD([sQuery(id+"F0.wireOp",EDGE,"E62.0.MirrorCS"),sQuery(id+"F0.wireOp",EDGE,"E67")])],"isStart":false});
            var Q56;
            {var subQ0=sQuery(id+"F0.wireOp",EDGE,"E56.trimOffspring");Q56=makeQuery(id+"F6.opFillet","BLEND_EDGE",EDGE,{"blendedFrom":[makeQuery(id+"F1.opExtrude","CAP_EDGE",EDGE,{"disambiguationData":[OSD([sQuery(id+"F0.wireOp",EDGE,"E0")])],"isStart":false}),makeQuery(id+"F1.opExtrude","SWEPT_FACE",FACE,{"disambiguationData":[OSD([subQ0]),TDD([makeQuery(id+"F0.imprint","IMPRINT",EDGE,{"disambiguationData":[TD([[makeQuery(id+"F0.imprint","INTERSECT",VERTEX,{"derivedFrom":[subQ0,sQuery(id+"F0.wireOp",EDGE,"E68")]}),-1.0]])],"derivedFrom":subQ0})])]})],"blendedInto":[makeQuery(id+"F1.opExtrude","SWEPT_FACE",FACE,{"disambiguationData":[OSD([subQ0]),TDD([makeQuery(id+"F0.imprint","IMPRINT",EDGE,{"disambiguationData":[TD([[makeQuery(id+"F0.imprint","INTERSECT",VERTEX,{"derivedFrom":[subQ0,sQuery(id+"F0.wireOp",EDGE,"E68")]}),-1.0]])],"derivedFrom":subQ0})])]})]});}
            var Q57;
            {var subQ0=sQuery(id+"F0.wireOp",EDGE,"E56.trimOffspring");Q57=makeQuery(id+"F6.opFillet","BLEND_EDGE",EDGE,{"blendedFrom":[makeQuery(id+"F1.opExtrude","CAP_EDGE",EDGE,{"disambiguationData":[OSD([sQuery(id+"F0.wireOp",EDGE,"E0")])],"isStart":false}),makeQuery(id+"F1.opExtrude","SWEPT_FACE",FACE,{"disambiguationData":[OSD([subQ0]),TDD([makeQuery(id+"F0.imprint","IMPRINT",EDGE,{"disambiguationData":[TD([[makeQuery(id+"F0.imprint","INTERSECT",VERTEX,{"derivedFrom":[subQ0,sQuery(id+"F0.wireOp",EDGE,"E70")]}),-1.0]])],"derivedFrom":subQ0})])]})],"blendedInto":[makeQuery(id+"F1.opExtrude","SWEPT_FACE",FACE,{"disambiguationData":[OSD([subQ0]),TDD([makeQuery(id+"F0.imprint","IMPRINT",EDGE,{"disambiguationData":[TD([[makeQuery(id+"F0.imprint","INTERSECT",VERTEX,{"derivedFrom":[subQ0,sQuery(id+"F0.wireOp",EDGE,"E70")]}),-1.0]])],"derivedFrom":subQ0})])]})]});}
            var Q58;
            Q58=makeQuery(id+"F6.opFillet","BLEND_EDGE",EDGE,{"blendedFrom":[makeQuery(id+"F1.opExtrude","CAP_EDGE",EDGE,{"disambiguationData":[OSD([sQuery(id+"F0.wireOp",EDGE,"E0")])],"isStart":false}),makeQuery(id+"F1.opExtrude","SWEPT_FACE",FACE,{"disambiguationData":[OSD([sQuery(id+"F0.wireOp",EDGE,"E1")])]})],"blendedInto":[makeQuery(id+"F1.opExtrude","SWEPT_FACE",FACE,{"disambiguationData":[OSD([sQuery(id+"F0.wireOp",EDGE,"E1")])]})]});
            var Q59;
            Q59=makeQuery(id+"F1.opExtrude","CAP_EDGE",EDGE,{"disambiguationData":[OSD([sQuery(id+"F0.wireOp",EDGE,"E76")])],"isStart":false});
            var Q60;
            Q60=makeQuery(id+"F1.opExtrude","CAP_EDGE",EDGE,{"disambiguationData":[OSD([sQuery(id+"F0.wireOp",EDGE,"E77")])],"isStart":false});
            var Q61;
            {var subQ0=sQuery(id+"F0.wireOp",EDGE,"E54.trimOffspring");Q61=makeQuery(id+"F6.opFillet","BLEND_EDGE",EDGE,{"blendedFrom":[makeQuery(id+"F1.opExtrude","CAP_EDGE",EDGE,{"disambiguationData":[OSD([sQuery(id+"F0.wireOp",EDGE,"E0")])],"isStart":false}),makeQuery(id+"F1.opExtrude","SWEPT_FACE",FACE,{"disambiguationData":[OSD([subQ0]),TDD([makeQuery(id+"F0.imprint","IMPRINT",EDGE,{"disambiguationData":[TD([[makeQuery(id+"F0.imprint","INTERSECT",VERTEX,{"derivedFrom":[subQ0,sQuery(id+"F0.wireOp",EDGE,"E73")]}),-1.0]])],"derivedFrom":subQ0})])]})],"blendedInto":[makeQuery(id+"F1.opExtrude","SWEPT_FACE",FACE,{"disambiguationData":[OSD([subQ0]),TDD([makeQuery(id+"F0.imprint","IMPRINT",EDGE,{"disambiguationData":[TD([[makeQuery(id+"F0.imprint","INTERSECT",VERTEX,{"derivedFrom":[subQ0,sQuery(id+"F0.wireOp",EDGE,"E73")]}),-1.0]])],"derivedFrom":subQ0})])]})]});}
            var Q62;
            {var subQ0=sQuery(id+"F0.wireOp",EDGE,"E54.trimOffspring");Q62=makeQuery(id+"F6.opFillet","BLEND_EDGE",EDGE,{"blendedFrom":[makeQuery(id+"F1.opExtrude","CAP_EDGE",EDGE,{"disambiguationData":[OSD([sQuery(id+"F0.wireOp",EDGE,"E0")])],"isStart":false}),makeQuery(id+"F1.opExtrude","SWEPT_FACE",FACE,{"disambiguationData":[OSD([subQ0]),TDD([makeQuery(id+"F0.imprint","IMPRINT",EDGE,{"disambiguationData":[TD([[makeQuery(id+"F0.imprint","INTERSECT",VERTEX,{"derivedFrom":[subQ0,sQuery(id+"F0.wireOp",EDGE,"E76")]}),1.0]])],"derivedFrom":subQ0})])]})],"blendedInto":[makeQuery(id+"F1.opExtrude","SWEPT_FACE",FACE,{"disambiguationData":[OSD([subQ0]),TDD([makeQuery(id+"F0.imprint","IMPRINT",EDGE,{"disambiguationData":[TD([[makeQuery(id+"F0.imprint","INTERSECT",VERTEX,{"derivedFrom":[subQ0,sQuery(id+"F0.wireOp",EDGE,"E76")]}),1.0]])],"derivedFrom":subQ0})])]})]});}
            var Q63;
            {var subQ0=sQuery(id+"F0.wireOp",EDGE,"E54.trimOffspring");Q63=makeQuery(id+"F6.opFillet","BLEND_EDGE",EDGE,{"blendedFrom":[makeQuery(id+"F1.opExtrude","CAP_EDGE",EDGE,{"disambiguationData":[OSD([sQuery(id+"F0.wireOp",EDGE,"E0")])],"isStart":false}),makeQuery(id+"F1.opExtrude","SWEPT_FACE",FACE,{"disambiguationData":[OSD([subQ0]),TDD([makeQuery(id+"F0.imprint","IMPRINT",EDGE,{"disambiguationData":[TD([[makeQuery(id+"F0.imprint","INTERSECT",VERTEX,{"derivedFrom":[subQ0,sQuery(id+"F0.wireOp",EDGE,"E77")]}),-1.0]])],"derivedFrom":subQ0})])]})],"blendedInto":[makeQuery(id+"F1.opExtrude","SWEPT_FACE",FACE,{"disambiguationData":[OSD([subQ0]),TDD([makeQuery(id+"F0.imprint","IMPRINT",EDGE,{"disambiguationData":[TD([[makeQuery(id+"F0.imprint","INTERSECT",VERTEX,{"derivedFrom":[subQ0,sQuery(id+"F0.wireOp",EDGE,"E77")]}),-1.0]])],"derivedFrom":subQ0})])]})]});}
            var Q64;
            {var subQ0=sQuery(id+"F0.wireOp",EDGE,"E54.trimOffspring");Q64=makeQuery(id+"F6.opFillet","BLEND_EDGE",EDGE,{"blendedFrom":[makeQuery(id+"F1.opExtrude","CAP_EDGE",EDGE,{"disambiguationData":[OSD([sQuery(id+"F0.wireOp",EDGE,"E0")])],"isStart":false}),makeQuery(id+"F1.opExtrude","SWEPT_FACE",FACE,{"disambiguationData":[OSD([subQ0]),TDD([makeQuery(id+"F0.imprint","IMPRINT",EDGE,{"disambiguationData":[TD([[makeQuery(id+"F0.imprint","INTERSECT",VERTEX,{"derivedFrom":[subQ0,sQuery(id+"F0.wireOp",EDGE,"E79.0.MirrorCS")]}),-1.0]])],"derivedFrom":subQ0})])]})],"blendedInto":[makeQuery(id+"F1.opExtrude","SWEPT_FACE",FACE,{"disambiguationData":[OSD([subQ0]),TDD([makeQuery(id+"F0.imprint","IMPRINT",EDGE,{"disambiguationData":[TD([[makeQuery(id+"F0.imprint","INTERSECT",VERTEX,{"derivedFrom":[subQ0,sQuery(id+"F0.wireOp",EDGE,"E79.0.MirrorCS")]}),-1.0]])],"derivedFrom":subQ0})])]})]});}
            fillet(context, id + "F7", {"entities" : qUnion([Q0, Q1, Q2, Q3, Q4, Q5, Q6, Q7, Q8, Q9, Q10, Q11, Q12, Q13, Q14, Q15, Q16, Q17, Q18, Q19, Q20, Q21, Q22, Q23, Q24, Q25, Q26, Q27, Q28, Q29, Q30, Q31, Q32, Q33, Q34, Q35, Q36, Q37, Q38, Q39, Q40, Q41, Q42, Q43, Q44, Q45, Q46, Q47, Q48, Q49, Q50, Q51, Q52, Q53, Q54, Q55, Q56, Q57, Q58, Q59, Q60, Q61, Q62, Q63, Q64]), "radius" : .5 * mm, "tangentPropagation" : true, "allowEdgeOverflow" : false});
        }
        {
            var Q0;
            {var subQ3=sQuery(id+"F0.wireOp",EDGE,"E17");Q0=makeQuery(id+"F0.imprint","IMPRINT",FACE,{"disambiguationData":[TD([[makeQuery(id+"F0.imprint","IMPRINT",EDGE,{"derivedFrom":subQ3}),1.0]])]});}
            var Q1;
            {var subQ3=sQuery(id+"F0.wireOp",EDGE,"E29.0.MirrorCS");Q1=makeQuery(id+"F0.imprint","IMPRINT",FACE,{"disambiguationData":[TD([[makeQuery(id+"F0.imprint","IMPRINT",EDGE,{"derivedFrom":subQ3}),-1.0]])]});}
            extrude(context, id + "F8", {"entities" : qUnion([Q0, Q1]), "operationType" : NewBodyOperationType.ADD, "depth" : 3.5 * mm});
        }
        {
            var Q0;
            Q0=makeQuery(id+"F1.opExtrude","SWEPT_BODY",BODY,{"disambiguationData":[OSD([sQuery(id+"F0.wireOp",EDGE,"E0"),sQuery(id+"F0.wireOp",EDGE,"E1"),sQuery(id+"F0.wireOp",EDGE,"E2"),sQuery(id+"F0.wireOp",EDGE,"E3.0.MirrorCS"),sQuery(id+"F0.wireOp",EDGE,"E4"),sQuery(id+"F0.wireOp",EDGE,"E5"),sQuery(id+"F0.wireOp",EDGE,"E6"),sQuery(id+"F0.wireOp",EDGE,"E7"),sQuery(id+"F0.wireOp",EDGE,"E8"),sQuery(id+"F0.wireOp",EDGE,"E9"),sQuery(id+"F0.wireOp",EDGE,"E10.0.MirrorCS"),sQuery(id+"F0.wireOp",EDGE,"E11.0.MirrorCS"),sQuery(id+"F0.wireOp",EDGE,"E12.0.MirrorCS"),sQuery(id+"F0.wireOp",EDGE,"E13.0.MirrorCS"),sQuery(id+"F0.wireOp",EDGE,"E14"),sQuery(id+"F0.wireOp",EDGE,"E15"),sQuery(id+"F0.wireOp",EDGE,"E16"),sQuery(id+"F0.wireOp",EDGE,"E17"),sQuery(id+"F0.wireOp",EDGE,"E18"),sQuery(id+"F0.wireOp",EDGE,"E19"),sQuery(id+"F0.wireOp",EDGE,"E21"),sQuery(id+"F0.wireOp",EDGE,"E22"),sQuery(id+"F0.wireOp",EDGE,"E24.filletArc"),sQuery(id+"F0.wireOp",EDGE,"E25.filletArc"),sQuery(id+"F0.wireOp",EDGE,"E26.0.MirrorCS"),sQuery(id+"F0.wireOp",EDGE,"E27.0.MirrorCS"),sQuery(id+"F0.wireOp",EDGE,"E28.0.MirrorCS"),sQuery(id+"F0.wireOp",EDGE,"E29.0.MirrorCS"),sQuery(id+"F0.wireOp",EDGE,"E30.0.MirrorCS"),sQuery(id+"F0.wireOp",EDGE,"E31.0.MirrorCS"),sQuery(id+"F0.wireOp",EDGE,"E32.0.MirrorCS"),sQuery(id+"F0.wireOp",EDGE,"E33.0.MirrorCS"),sQuery(id+"F0.wireOp",EDGE,"E34.0.MirrorCS"),sQuery(id+"F0.wireOp",EDGE,"E35.0.MirrorCS"),sQuery(id+"F0.wireOp",EDGE,"E46.rect.left"),sQuery(id+"F0.wireOp",EDGE,"E46.rect.right"),sQuery(id+"F0.wireOp",EDGE,"E47.trimOffspring"),sQuery(id+"F0.wireOp",EDGE,"E48.0.MirrorCS"),sQuery(id+"F0.wireOp",EDGE,"E49.0.MirrorCS"),sQuery(id+"F0.wireOp",EDGE,"E50.trimOffspring"),sQuery(id+"F0.wireOp",EDGE,"E51.rect.left"),sQuery(id+"F0.wireOp",EDGE,"E51.rect.right"),sQuery(id+"F0.wireOp",EDGE,"E52"),sQuery(id+"F0.wireOp",EDGE,"E53"),sQuery(id+"F0.wireOp",EDGE,"E54.trimOffspring"),sQuery(id+"F0.wireOp",EDGE,"E55.trimOffspring"),sQuery(id+"F0.wireOp",EDGE,"E56.trimOffspring"),sQuery(id+"F0.wireOp",EDGE,"E57"),sQuery(id+"F0.wireOp",EDGE,"E58"),sQuery(id+"F0.wireOp",EDGE,"E59"),sQuery(id+"F0.wireOp",EDGE,"E60"),sQuery(id+"F0.wireOp",EDGE,"E61"),sQuery(id+"F0.wireOp",EDGE,"E62.0.MirrorCS"),sQuery(id+"F0.wireOp",EDGE,"E63.0.MirrorCS"),sQuery(id+"F0.wireOp",EDGE,"E64.0.MirrorCS"),sQuery(id+"F0.wireOp",EDGE,"E65.0.MirrorCS"),sQuery(id+"F0.wireOp",EDGE,"E66.0.MirrorCS"),sQuery(id+"F0.wireOp",EDGE,"E67"),sQuery(id+"F0.wireOp",EDGE,"E68"),sQuery(id+"F0.wireOp",EDGE,"E69"),sQuery(id+"F0.wireOp",EDGE,"E70"),sQuery(id+"F0.wireOp",EDGE,"E71"),sQuery(id+"F0.wireOp",EDGE,"E72"),sQuery(id+"F0.wireOp",EDGE,"E73"),sQuery(id+"F0.wireOp",EDGE,"E74"),sQuery(id+"F0.wireOp",EDGE,"E75"),sQuery(id+"F0.wireOp",EDGE,"E76"),sQuery(id+"F0.wireOp",EDGE,"E77"),sQuery(id+"F0.wireOp",EDGE,"E78.0.MirrorCS"),sQuery(id+"F0.wireOp",EDGE,"E79.0.MirrorCS"),sQuery(id+"F0.wireOp",EDGE,"E80.0.MirrorCS"),sQuery(id+"F0.wireOp",EDGE,"E81.0.MirrorCS"),sQuery(id+"F0.wireOp",EDGE,"E85"),sQuery(id+"F0.wireOp",EDGE,"E86.trimOffspring"),sQuery(id+"F0.wireOp",EDGE,"E87.trimOffspring")])]});
            var Q1;
            Q1=qCreatedBy(makeId("Origin.pointOp"),VERTEX);
            transform(context, id + "F9", {"entities" : qUnion([Q0]), "transformType" : TransformType.SCALE_UNIFORMLY, "scale" : 1.3, "makeCopy" : false, "scalePoint" : qUnion([Q1])});
        }
        {
            var Q0;
            Q0=makeQuery(id+"F1.opExtrude","SWEPT_EDGE",EDGE,{"disambiguationData":[OSD([sQuery(id+"F0.wireOp",EDGE,"E65.0.MirrorCS"),sQuery(id+"F0.wireOp",EDGE,"E66.0.MirrorCS")])]});
            var Q1;
            Q1=makeQuery(id+"F1.opExtrude","SWEPT_EDGE",EDGE,{"disambiguationData":[OSD([sQuery(id+"F0.wireOp",EDGE,"E63.0.MirrorCS"),sQuery(id+"F0.wireOp",EDGE,"E64.0.MirrorCS")])]});
            var Q2;
            Q2=makeQuery(id+"F1.opExtrude","SWEPT_EDGE",EDGE,{"disambiguationData":[OSD([sQuery(id+"F0.wireOp",EDGE,"E57"),sQuery(id+"F0.wireOp",EDGE,"E58")])]});
            var Q3;
            Q3=makeQuery(id+"F1.opExtrude","SWEPT_EDGE",EDGE,{"disambiguationData":[OSD([sQuery(id+"F0.wireOp",EDGE,"E59"),sQuery(id+"F0.wireOp",EDGE,"E60")])]});
            var Q4;
            Q4=makeQuery(id+"F1.opExtrude","SWEPT_EDGE",EDGE,{"disambiguationData":[OSD([sQuery(id+"F0.wireOp",EDGE,"E72"),sQuery(id+"F0.wireOp",EDGE,"E73")])]});
            var Q5;
            Q5=makeQuery(id+"F1.opExtrude","SWEPT_EDGE",EDGE,{"disambiguationData":[OSD([sQuery(id+"F0.wireOp",EDGE,"E80.0.MirrorCS"),sQuery(id+"F0.wireOp",EDGE,"E81.0.MirrorCS")])]});
            fillet(context, id + "F10", {"entities" : qUnion([Q0, Q1, Q2, Q3, Q4, Q5]), "radius" : .25 * mm, "tangentPropagation" : true, "allowEdgeOverflow" : false});
        }
        {
            var Q0;
            Q0=makeQuery(id+"F1.opExtrude","SWEPT_EDGE",EDGE,{"disambiguationData":[OSD([sQuery(id+"F0.wireOp",EDGE,"E78.0.MirrorCS"),sQuery(id+"F0.wireOp",EDGE,"E79.0.MirrorCS")])]});
            var Q1;
            Q1=makeQuery(id+"F1.opExtrude","SWEPT_EDGE",EDGE,{"disambiguationData":[OSD([sQuery(id+"F0.wireOp",EDGE,"E76"),sQuery(id+"F0.wireOp",EDGE,"E77")])]});
            var Q2;
            Q2=makeQuery(id+"F1.opExtrude","SWEPT_EDGE",EDGE,{"disambiguationData":[OSD([sQuery(id+"F0.wireOp",EDGE,"E74"),sQuery(id+"F0.wireOp",EDGE,"E75")])]});
            var Q3;
            Q3=makeQuery(id+"F1.opExtrude","SWEPT_EDGE",EDGE,{"disambiguationData":[OSD([sQuery(id+"F0.wireOp",EDGE,"E61"),sQuery(id+"F0.wireOp",EDGE,"E62.0.MirrorCS")])]});
            fillet(context, id + "F11", {"entities" : qUnion([Q0, Q1, Q2, Q3]), "radius" : .2 * mm, "tangentPropagation" : true, "allowEdgeOverflow" : false});
        }
    });
